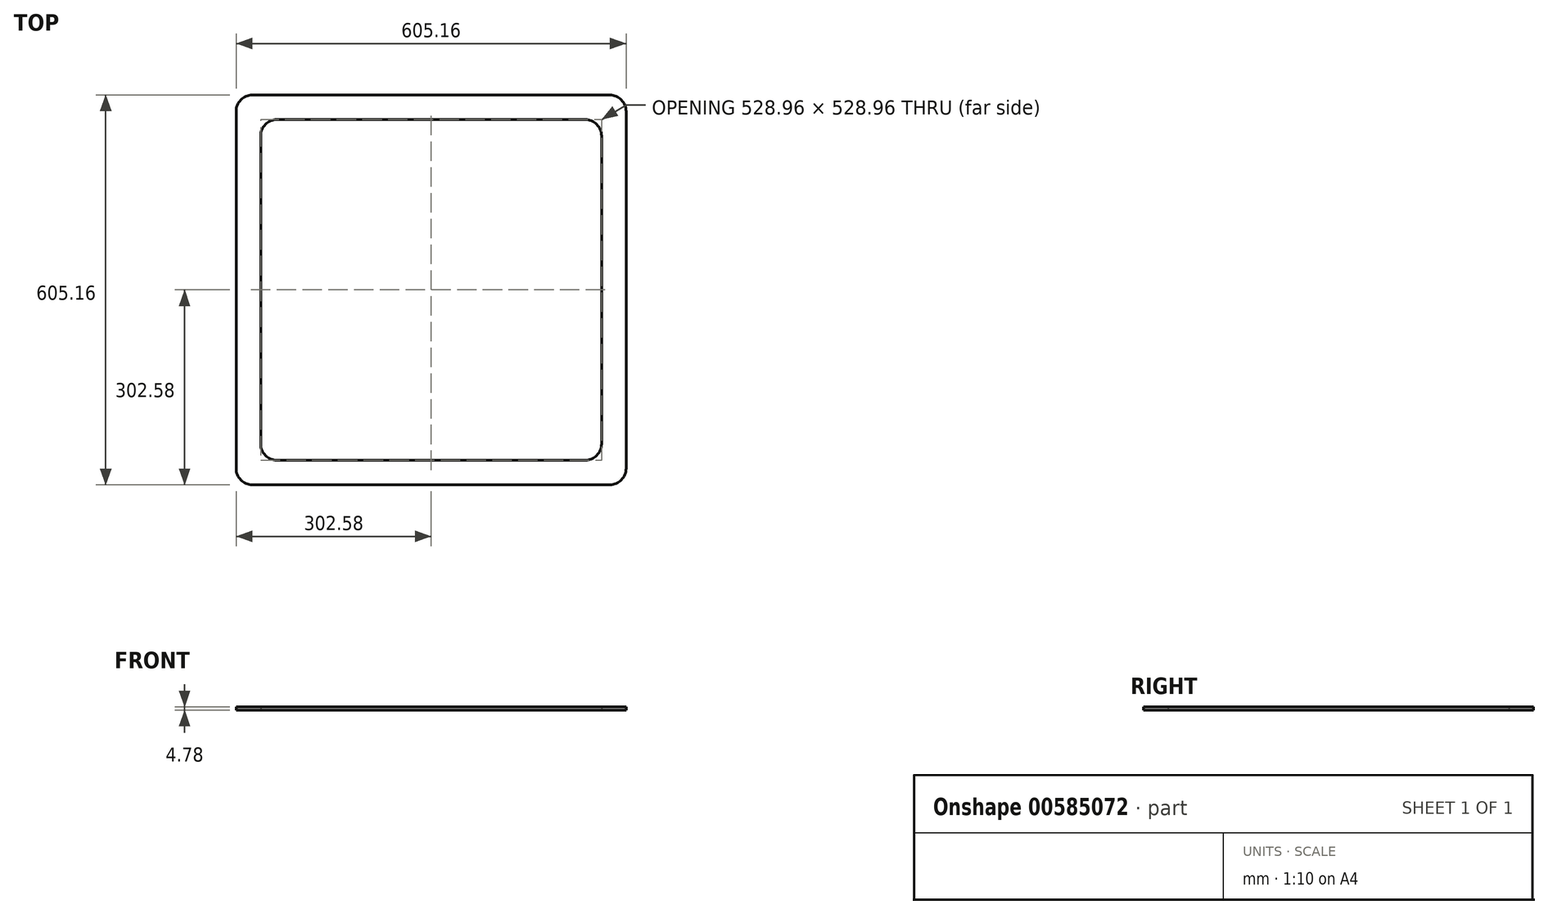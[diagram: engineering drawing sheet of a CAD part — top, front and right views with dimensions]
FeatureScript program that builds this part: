
annotation { "Feature Type Name" : "Feature", "Feature Type Description" : "" }
export const myFeature = defineFeature(function(context is Context, id is Id, definition is map)
    precondition{}
    {
        {
            var Q0;
            Q0=qCreatedBy(makeId("Top.planeOp"),FACE);
            var sketch = newSketch(context, id + "F0", { "sketchPlane" : qUnion([Q0])});
            skLineSegment(sketch, "E0.bottom", {"start": v(302.58, -302.58) * mm, "end": v(-302.58, -302.58) * mm});
            skLineSegment(sketch, "E0.top", {"start": v(302.58, 302.58) * mm, "end": v(-302.58, 302.58) * mm});
            skLineSegment(sketch, "E0.left", {"start": v(302.58, -302.58) * mm, "end": v(302.58, 302.58) * mm});
            skLineSegment(sketch, "E0.right", {"start": v(-302.58, -302.58) * mm, "end": v(-302.58, 302.58) * mm});
            skPoint(sketch, "E0.middle", {"position": v(0, 0) * mm});
            skLineSegment(sketch, "E1.0", {"start": v(264.48, 264.48) * mm, "end": v(-264.48, 264.48) * mm});
            skLineSegment(sketch, "E1.1", {"start": v(264.48, -264.48) * mm, "end": v(264.48, 264.48) * mm});
            skLineSegment(sketch, "E1.2", {"start": v(264.48, -264.48) * mm, "end": v(-264.48, -264.48) * mm});
            skLineSegment(sketch, "E1.3", {"start": v(-264.48, -264.48) * mm, "end": v(-264.48, 264.48) * mm});
            skSolve(sketch);
        }
        {
            var Q0;
            Q0 = qSketchRegion(id + "F0", true);
            extrude(context, id + "F1", {"entities" : qUnion([Q0]), "depth" : 4.78 * mm, "offsetDistance" : 25.4 * mm});
        }
        {
            var Q0;
            Q0=makeQuery(id+"F1.opExtrude","SWEPT_EDGE",EDGE,{"disambiguationData":[OSD([sQuery(id+"F0.wireOp",EDGE,"E0.bottom"),sQuery(id+"F0.wireOp",EDGE,"E0.right")])]});
            var Q1;
            Q1=makeQuery(id+"F1.opExtrude","SWEPT_EDGE",EDGE,{"disambiguationData":[OSD([sQuery(id+"F0.wireOp",EDGE,"E1.0"),sQuery(id+"F0.wireOp",EDGE,"E1.1")])]});
            var Q2;
            Q2=makeQuery(id+"F1.opExtrude","SWEPT_EDGE",EDGE,{"disambiguationData":[OSD([sQuery(id+"F0.wireOp",EDGE,"E0.bottom"),sQuery(id+"F0.wireOp",EDGE,"E0.left")])]});
            var Q3;
            Q3=makeQuery(id+"F1.opExtrude","SWEPT_EDGE",EDGE,{"disambiguationData":[OSD([sQuery(id+"F0.wireOp",EDGE,"E1.0"),sQuery(id+"F0.wireOp",EDGE,"E1.3")])]});
            var Q4;
            Q4=makeQuery(id+"F1.opExtrude","SWEPT_EDGE",EDGE,{"disambiguationData":[OSD([sQuery(id+"F0.wireOp",EDGE,"E0.top"),sQuery(id+"F0.wireOp",EDGE,"E0.left")])]});
            var Q5;
            Q5=makeQuery(id+"F1.opExtrude","SWEPT_EDGE",EDGE,{"disambiguationData":[OSD([sQuery(id+"F0.wireOp",EDGE,"E1.2"),sQuery(id+"F0.wireOp",EDGE,"E1.3")])]});
            var Q6;
            Q6=makeQuery(id+"F1.opExtrude","SWEPT_EDGE",EDGE,{"disambiguationData":[OSD([sQuery(id+"F0.wireOp",EDGE,"E0.top"),sQuery(id+"F0.wireOp",EDGE,"E0.right")])]});
            var Q7;
            Q7=makeQuery(id+"F1.opExtrude","SWEPT_EDGE",EDGE,{"disambiguationData":[OSD([sQuery(id+"F0.wireOp",EDGE,"E1.1"),sQuery(id+"F0.wireOp",EDGE,"E1.2")])]});
            fillet(context, id + "F2", {"entities" : qUnion([Q0, Q1, Q2, Q3, Q4, Q5, Q6, Q7]), "tangentPropagation" : true, "radius" : 25.4 * mm, "defaultsChanged" : true, "vertexSettings" : [], "allowEdgeOverflow" : false});
        }
    });
